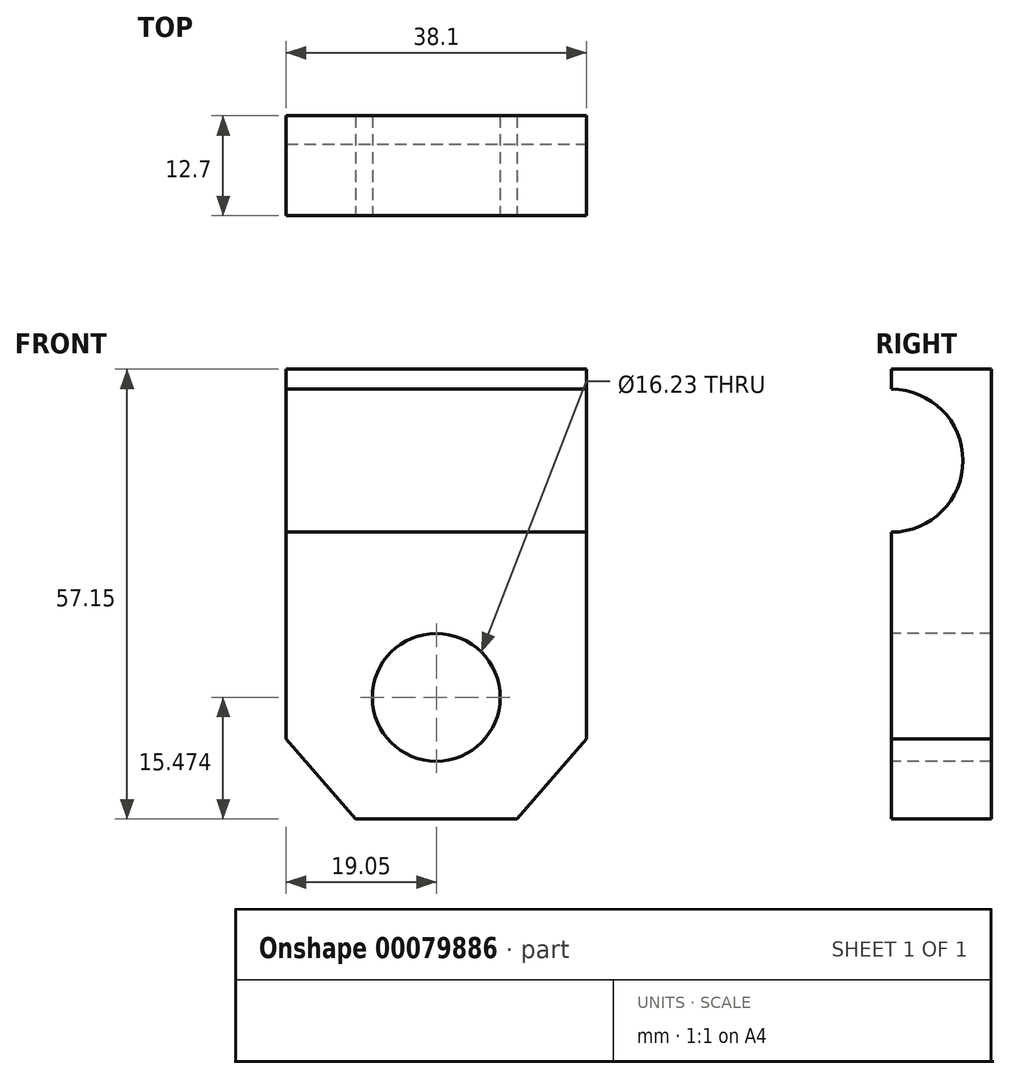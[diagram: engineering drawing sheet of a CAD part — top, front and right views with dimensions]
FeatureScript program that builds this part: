
annotation { "Feature Type Name" : "Feature", "Feature Type Description" : "" }
export const myFeature = defineFeature(function(context is Context, id is Id, definition is map)
    precondition{}
    {
        {
            var Q0;
            Q0=qCreatedBy(makeId("Front.planeOp"),FACE);
            var sketch = newSketch(context, id + "F0", { "sketchPlane" : qUnion([Q0])});
            skLineSegment(sketch, "E0.bottom", {"start": v(19.05, 28.58) * mm, "end": v(-19.05, 28.58) * mm});
            skLineSegment(sketch, "E0.top", {"start": v(19.05, -28.58) * mm, "end": v(-19.05, -28.58) * mm});
            skLineSegment(sketch, "E0.left", {"start": v(19.05, 28.58) * mm, "end": v(19.05, -28.58) * mm});
            skLineSegment(sketch, "E0.right", {"start": v(-19.05, 28.58) * mm, "end": v(-19.05, -28.58) * mm});
            skPoint(sketch, "E0.middle", {"position": v(0, 0) * mm});
            skSolve(sketch);
        }
        {
            var Q0;
            Q0=makeQuery(id+"F0.imprint","IMPRINT",FACE,{"disambiguationData":[TD([[makeQuery(id+"F0.imprint","IMPRINT",EDGE,{"derivedFrom":sQuery(id+"F0.wireOp",EDGE,"E0.bottom")}),1.0]])]});
            extrude(context, id + "F1", {"entities" : qUnion([Q0]), "depth" : 12.7 * mm});
        }
        {
            var Q0;
            Q0=makeQuery(id+"F1.opExtrude","CAP_FACE",FACE,{"disambiguationData":[OSD([sQuery(id+"F0.wireOp",EDGE,"E0.bottom"),sQuery(id+"F0.wireOp",EDGE,"E0.top"),sQuery(id+"F0.wireOp",EDGE,"E0.left"),sQuery(id+"F0.wireOp",EDGE,"E0.right")])],"isStart":false});
            var sketch = newSketch(context, id + "F2", { "sketchPlane" : qUnion([Q0])});
            skLineSegment(sketch, "E1", {"start": v(10.26, -28.58) * mm, "end": v(19.05, -18.42) * mm});
            skLineSegment(sketch, "E2", {"start": v(19.05, -18.42) * mm, "end": v(19.05, -28.58) * mm});
            skLineSegment(sketch, "E3", {"start": v(19.05, -28.58) * mm, "end": v(10.26, -28.58) * mm});
            skLineSegment(sketch, "E4.MirrorCS", {"start": v(-10.26, -28.58) * mm, "end": v(-19.05, -18.42) * mm});
            skLineSegment(sketch, "E5.MirrorCS", {"start": v(-19.05, -18.42) * mm, "end": v(-19.05, -28.58) * mm});
            skLineSegment(sketch, "E6.MirrorCS", {"start": v(-19.05, -28.58) * mm, "end": v(-10.26, -28.58) * mm});
            skSolve(sketch);
        }
        {
            var Q0;
            Q0 = qSketchRegion(id + "F2", true);
            extrude(context, id + "F3", {"entities" : qUnion([Q0]), "operationType" : NewBodyOperationType.REMOVE, "oppositeDirection" : true, "depth" : 25.4 * mm});
        }
        {
            var Q0;
            Q0=makeQuery(id+"F1.opExtrude","SWEPT_FACE",FACE,{"disambiguationData":[OSD([sQuery(id+"F0.wireOp",EDGE,"E0.left")])]});
            var sketch = newSketch(context, id + "F4", { "sketchPlane" : qUnion([Q0])});
            skSolve(sketch);
        }
        {
            var Q0;
            {var subQ0=sQuery(id+"F0.wireOp",EDGE,"E0.left");Q0=makeQuery(id+"F4.imprint","IMPRINT",FACE,{"disambiguationData":[TD([[makeQuery(id+"F4.imprint","IMPRINT",EDGE,{"derivedFrom":makeQuery(id+"F1.opExtrude","CAP_EDGE",EDGE,{"disambiguationData":[OSD([subQ0])],"isStart":true})}),-1.0]])]});}
            var sketch = newSketch(context, id + "F5", { "sketchPlane" : qUnion([Q0])});
            skCircle(sketch, "E7", {"center": v(-12.7, 16.96) * mm, "radius": 9.08 * mm});
            skSolve(sketch);
        }
        {
            var Q0;
            {var subQ0=sQuery(id+"F5.wireOp",EDGE,"E7");var subQ1=makeQuery(id+"F4.imprint","IMPRINT",EDGE,{"derivedFrom":makeQuery(id+"F1.opExtrude","CAP_EDGE",EDGE,{"disambiguationData":[OSD([sQuery(id+"F0.wireOp",EDGE,"E0.left")])],"isStart":false})});var subQ2=makeQuery(id+"F5.imprint","INTERSECT",VERTEX,{"disambiguationData":[OD(0.0)],"derivedFrom":[subQ1,subQ0]});Q0=makeQuery(id+"F5.imprint","IMPRINT",FACE,{"disambiguationData":[TD([[makeQuery(id+"F5.imprint","IMPRINT",EDGE,{"disambiguationData":[TD([[subQ2,1.0]])],"derivedFrom":subQ0}),1.0]])]});}
            var sketch = newSketch(context, id + "F6", { "sketchPlane" : qUnion([Q0])});
            skSolve(sketch);
        }
        {
            var Q0;
            Q0 = qSketchRegion(id + "F6", true);
            var Q1;
            {var subQ0=sQuery(id+"F5.wireOp",EDGE,"E7");var subQ1=makeQuery(id+"F4.imprint","IMPRINT",EDGE,{"derivedFrom":makeQuery(id+"F1.opExtrude","CAP_EDGE",EDGE,{"disambiguationData":[OSD([sQuery(id+"F0.wireOp",EDGE,"E0.left")])],"isStart":false})});var subQ2=makeQuery(id+"F5.imprint","INTERSECT",VERTEX,{"disambiguationData":[OD(0.0)],"derivedFrom":[subQ1,subQ0]});Q1=makeQuery(id+"F5.imprint","IMPRINT",FACE,{"disambiguationData":[TD([[makeQuery(id+"F5.imprint","IMPRINT",EDGE,{"disambiguationData":[TD([[subQ2,-1.0]])],"derivedFrom":subQ0}),1.0]])]});}
            var Q2;
            {var subQ0=sQuery(id+"F5.wireOp",EDGE,"E7");var subQ1=makeQuery(id+"F4.imprint","IMPRINT",EDGE,{"derivedFrom":makeQuery(id+"F1.opExtrude","CAP_EDGE",EDGE,{"disambiguationData":[OSD([sQuery(id+"F0.wireOp",EDGE,"E0.left")])],"isStart":false})});var subQ2=makeQuery(id+"F5.imprint","INTERSECT",VERTEX,{"disambiguationData":[OD(0.0)],"derivedFrom":[subQ1,subQ0]});Q2=makeQuery(id+"F5.imprint","IMPRINT",FACE,{"disambiguationData":[TD([[makeQuery(id+"F5.imprint","IMPRINT",EDGE,{"disambiguationData":[TD([[subQ2,1.0]])],"derivedFrom":subQ0}),1.0]])]});}
            extrude(context, id + "F7", {"entities" : qUnion([Q0, Q1, Q2]), "operationType" : NewBodyOperationType.REMOVE, "oppositeDirection" : true, "depth" : 101.6 * mm});
        }
        {
            var Q0;
            Q0=makeQuery(id+"F1.opExtrude","CAP_FACE",FACE,{"disambiguationData":[OSD([sQuery(id+"F0.wireOp",EDGE,"E0.bottom"),sQuery(id+"F0.wireOp",EDGE,"E0.top"),sQuery(id+"F0.wireOp",EDGE,"E0.left"),sQuery(id+"F0.wireOp",EDGE,"E0.right")])],"isStart":true});
            var sketch = newSketch(context, id + "F8", { "sketchPlane" : qUnion([Q0])});
            skSolve(sketch);
        }
        {
            var Q0;
            Q0 = qSketchRegion(id + "F8", true);
            var Q1;
            {var subQ3=sQuery(id+"F0.wireOp",EDGE,"E0.bottom");Q1=makeQuery(id+"F8.imprint","IMPRINT",FACE,{"disambiguationData":[TD([[makeQuery(id+"F8.imprint","IMPRINT",EDGE,{"derivedFrom":makeQuery(id+"F1.opExtrude","CAP_EDGE",EDGE,{"disambiguationData":[OSD([subQ3])],"isStart":true})}),-1.0]])]});}
            extrude(context, id + "F9", {"entities" : qUnion([Q0, Q1]), "operationType" : NewBodyOperationType.ADD, "oppositeDirection" : true, "depth" : 2.54 * mm});
        }
        {
            var Q0;
            {var subQ0=sQuery(id+"F0.wireOp",EDGE,"E0.right");var subQ1=sQuery(id+"F0.wireOp",EDGE,"E0.left");var subQ2=sQuery(id+"F0.wireOp",EDGE,"E0.top");Q0=makeQuery(id+"F7.boolean.opBoolean","SPLIT",FACE,{"disambiguationData":[TD([makeQuery(id+"F1.opExtrude","SWEPT_FACE",FACE,{"disambiguationData":[OSD([subQ2])]})])],"derivedFrom":makeQuery(id+"F1.opExtrude","CAP_FACE",FACE,{"disambiguationData":[OSD([sQuery(id+"F0.wireOp",EDGE,"E0.bottom"),subQ2,subQ1,subQ0])],"isStart":false})});}
            var sketch = newSketch(context, id + "F10", { "sketchPlane" : qUnion([Q0])});
            skCircle(sketch, "E8", {"center": v(0, -13.1) * mm, "radius": 8.11 * mm});
            skSolve(sketch);
        }
        {
            var Q0;
            Q0=makeQuery(id+"F10.imprint","IMPRINT",FACE,{"disambiguationData":[TD([[makeQuery(id+"F10.imprint","IMPRINT",EDGE,{"derivedFrom":sQuery(id+"F10.wireOp",EDGE,"E8")}),1.0]])]});
            extrude(context, id + "F11", {"entities" : qUnion([Q0]), "operationType" : NewBodyOperationType.REMOVE, "oppositeDirection" : true, "depth" : 25.4 * mm});
        }
    });
